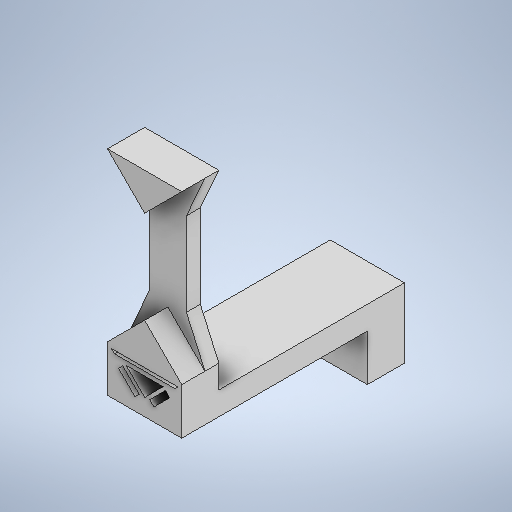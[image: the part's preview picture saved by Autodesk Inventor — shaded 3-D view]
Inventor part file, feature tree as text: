
AUTODESK INVENTOR PART (.ipt)
format: ipt  version: 2025.2 (Build 292293000, 293)  size: 318,464 bytes
history: native  units: mm
features: extrude x7, sketch x6
ambient origin geometry x8: Origin, YZ Plane, XZ Plane, XY Plane, X Axis, Y Axis, Z Axis, Center Point
bodies: Solid1 (feature_tree)
feature tree (13):
  sketch  "Sketch1"  dims[d0=20.0mm d1=16.0mm]
  extrude  "Extrusion1"  Depth=16.0mm
  extrude  "Extrusion2"  Depth=5.0mm TaperAngle=0.0deg
  extrude  "Extrusion3"  Depth=13.0mm
  extrude  "Extrusion4"  Depth=4.0mm
  extrude  "Extrusion5"  TaperAngle=45.0deg  [1 undecoded]
  extrude  "Extrusion6"  Depth=3.0mm TaperAngle=0.0deg
  extrude  "Extrusion7"  Depth=10.0mm TaperAngle=0.0deg
  sketch  "Sketch2"  dims[d3=5.0mm d4=5.0mm d5=0.0mm]
  sketch  "Sketch3"  dims[d7=1.5mm d9=13.0mm]
  sketch  "Sketch4"  dims[d10=4.0mm d11=0.0mm d12=36.0mm]
  sketch  "Sketch5"  dims[d13=90.0deg d14=45.0deg]
  sketch  "Sketch6"  dims[d15=5.0mm d16=0.0mm d17=3.0mm d18=0.0mm d19=10.0mm d20=0.0mm d21=5.0mm d22=40.0mm d23=0.0mm d24=8.0mm d25=10.0mm d26=0.0mm]
note: 1 required parameter value undecoded (feature->parameter linkage not recoverable at this tier; creation-order binding heuristic only, values carry confidence <= 0.55)
